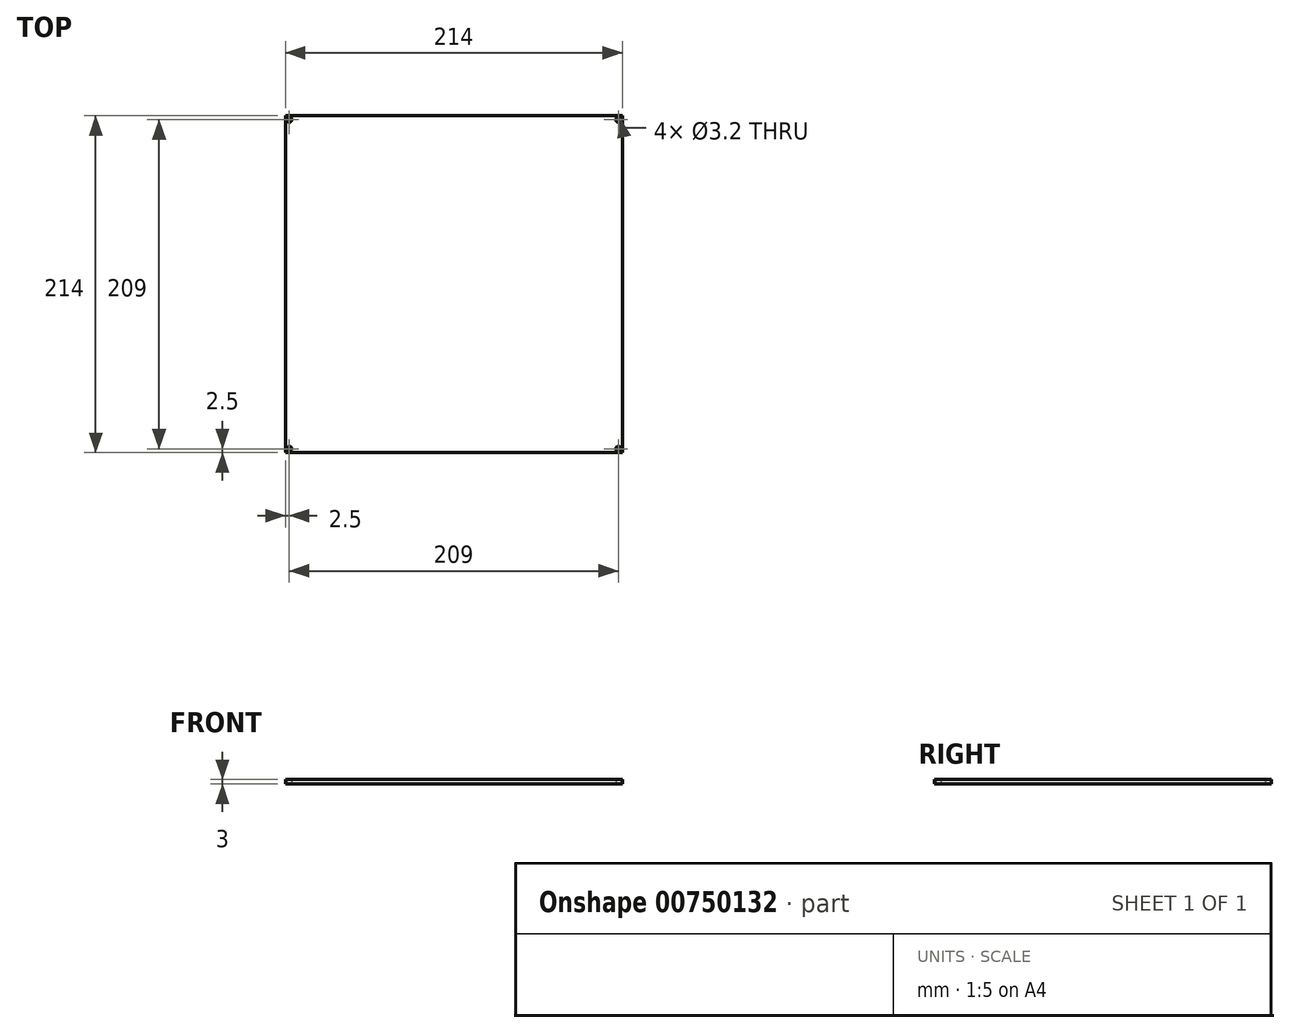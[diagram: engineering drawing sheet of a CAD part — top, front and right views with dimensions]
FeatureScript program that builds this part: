
annotation { "Feature Type Name" : "Feature", "Feature Type Description" : "" }
export const myFeature = defineFeature(function(context is Context, id is Id, definition is map)
    precondition{}
    {
        {
            var Q0;
            Q0=qCreatedBy(makeId("Top.planeOp"),FACE);
            var sketch = newSketch(context, id + "F0", { "sketchPlane" : qUnion([Q0])});
            skLineSegment(sketch, "E0.bottom", {"start": v(107, 107) * mm, "end": v(-107, 107) * mm});
            skLineSegment(sketch, "E0.top", {"start": v(107, -107) * mm, "end": v(-107, -107) * mm});
            skLineSegment(sketch, "E0.left", {"start": v(107, 107) * mm, "end": v(107, -107) * mm});
            skLineSegment(sketch, "E0.right", {"start": v(-107, 107) * mm, "end": v(-107, -107) * mm});
            skPoint(sketch, "E0.middle", {"position": v(0, 0) * mm});
            skCircle(sketch, "E1", {"center": v(-104.5, 104.5) * mm, "radius": 1.6 * mm});
            skCircle(sketch, "E2.MirrorC", {"center": v(104.5, 104.5) * mm, "radius": 1.6 * mm});
            skCircle(sketch, "E3.MirrorC", {"center": v(-104.5, -104.5) * mm, "radius": 1.6 * mm});
            skCircle(sketch, "E4.MirrorC", {"center": v(104.5, -104.5) * mm, "radius": 1.6 * mm});
            skSolve(sketch);
        }
        {
            var Q0;
            Q0=makeQuery(id+"F0.imprint","IMPRINT",FACE,{"disambiguationData":[TD([[makeQuery(id+"F0.imprint","IMPRINT",EDGE,{"derivedFrom":sQuery(id+"F0.wireOp",EDGE,"E0.bottom")}),1.0]])]});
            extrude(context, id + "F1", {"entities" : qUnion([Q0]), "depth" : 3 * mm, "offsetDistance" : 25 * mm});
        }
    });
